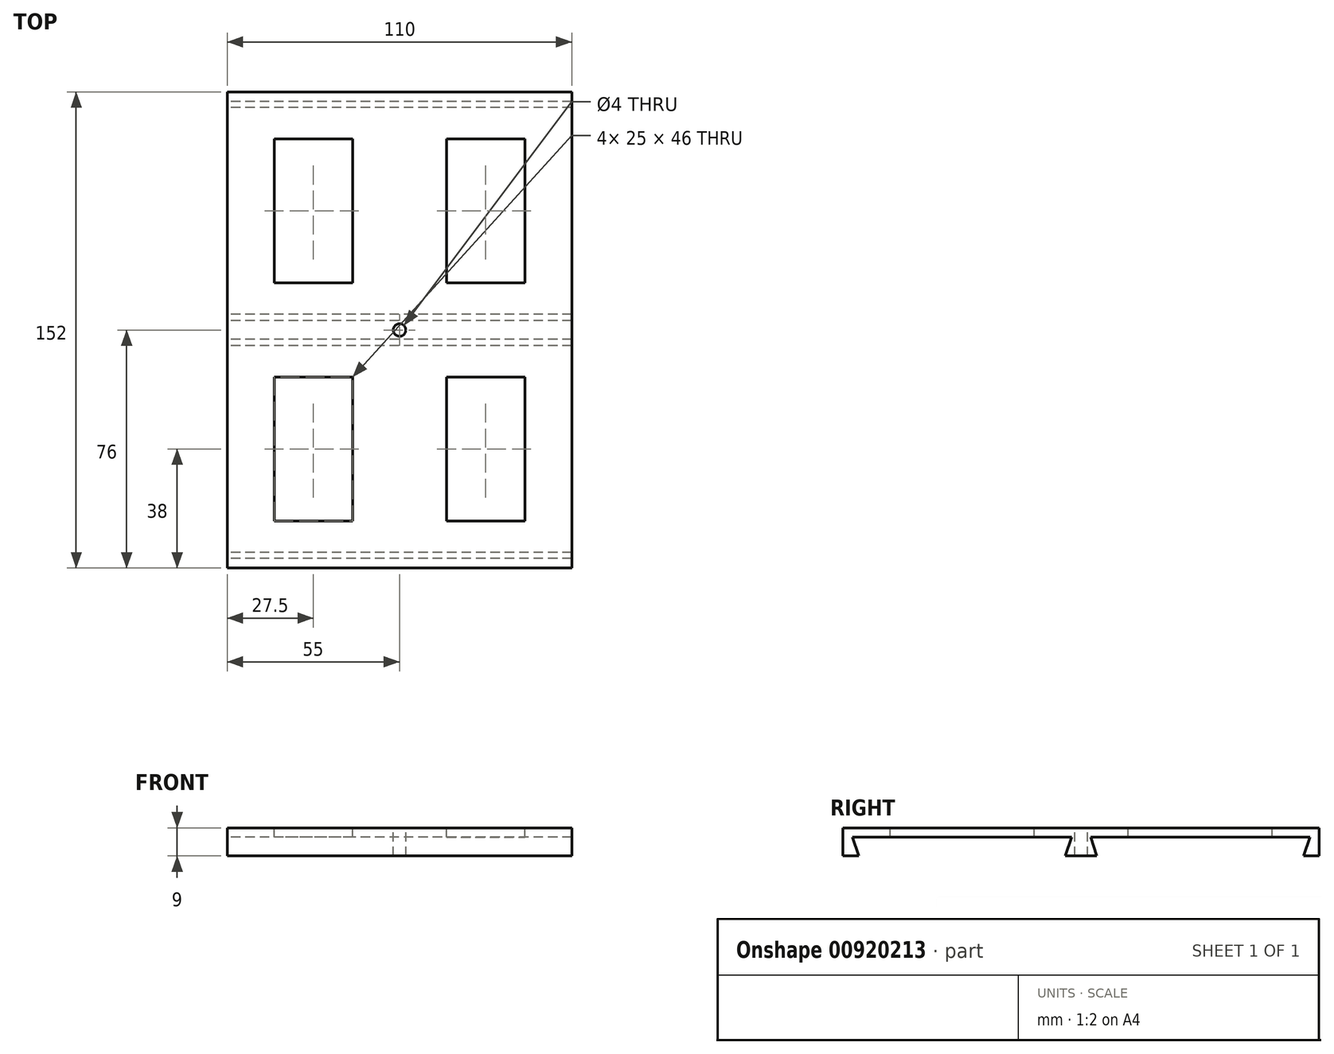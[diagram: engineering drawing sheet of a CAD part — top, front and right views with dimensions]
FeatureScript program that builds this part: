
annotation { "Feature Type Name" : "Feature", "Feature Type Description" : "" }
export const myFeature = defineFeature(function(context is Context, id is Id, definition is map)
    precondition{}
    {
        {
            var Q0;
            Q0=qCreatedBy(makeId("Right.planeOp"),FACE);
            var sketch = newSketch(context, id + "F0", { "sketchPlane" : qUnion([Q0])});
            skLineSegment(sketch, "E0", {"start": v(0, -9) * mm, "end": v(-5, -9) * mm});
            skLineSegment(sketch, "E1", {"start": v(0, 0) * mm, "end": v(-76, 0) * mm});
            skLineSegment(sketch, "E2", {"start": v(0, 0) * mm, "end": v(-3, 0) * mm});
            skLineSegment(sketch, "E3", {"start": v(-3, -3) * mm, "end": v(-5, -9) * mm});
            skLineSegment(sketch, "E4", {"start": v(-3, -3) * mm, "end": v(-73, -3) * mm});
            skLineSegment(sketch, "E5", {"start": v(-73, -9) * mm, "end": v(-71, -9) * mm});
            skLineSegment(sketch, "E6", {"start": v(-71, -9) * mm, "end": v(-73, -3) * mm});
            skLineSegment(sketch, "E7", {"start": v(-76, 0) * mm, "end": v(-76, -9) * mm});
            skLineSegment(sketch, "E8", {"start": v(-76, -9) * mm, "end": v(-73, -9) * mm});
            skLineSegment(sketch, "E9.MirrorCS", {"start": v(0, 0) * mm, "end": v(3, 0) * mm});
            skLineSegment(sketch, "E10.MirrorCS", {"start": v(73, -9) * mm, "end": v(71, -9) * mm});
            skLineSegment(sketch, "E11.MirrorCS", {"start": v(0, -9) * mm, "end": v(5, -9) * mm});
            skLineSegment(sketch, "E12.MirrorCS", {"start": v(76, -9) * mm, "end": v(73, -9) * mm});
            skLineSegment(sketch, "E13.MirrorCS", {"start": v(3, -3) * mm, "end": v(73, -3) * mm});
            skLineSegment(sketch, "E14.MirrorCS", {"start": v(71, -9) * mm, "end": v(73, -3) * mm});
            skLineSegment(sketch, "E15.MirrorCS", {"start": v(3, -3) * mm, "end": v(5, -9) * mm});
            skLineSegment(sketch, "E16.MirrorCS", {"start": v(76, 0) * mm, "end": v(76, -9) * mm});
            skLineSegment(sketch, "E17.MirrorCS", {"start": v(0, 0) * mm, "end": v(76, 0) * mm});
            skSolve(sketch);
        }
        {
            var Q0;
            Q0=makeQuery(id+"F0.imprint","IMPRINT",FACE,{"disambiguationData":[TD([[makeQuery(id+"F0.imprint","IMPRINT",EDGE,{"derivedFrom":sQuery(id+"F0.wireOp",EDGE,"E0")}),-1.0]])]});
            extrude(context, id + "F1", {"entities" : qUnion([Q0]), "depth" : 110 * mm, "offsetDistance" : 25 * mm});
        }
        {
            var Q0;
            Q0=makeQuery(id+"F1.opExtrude","SWEPT_FACE",FACE,{"disambiguationData":[OSD([sQuery(id+"F0.wireOp",EDGE,"E1"),sQuery(id+"F0.wireOp",EDGE,"E2"),sQuery(id+"F0.wireOp",EDGE,"E17.MirrorCS")])]});
            var sketch = newSketch(context, id + "F2", { "sketchPlane" : qUnion([Q0])});
            skLineSegment(sketch, "E18", {"start": v(0, 0) * mm, "end": v(110, 0) * mm, "construction": true});
            skLineSegment(sketch, "E19", {"start": v(55, -76) * mm, "end": v(55, 76) * mm, "construction": true});
            skLineSegment(sketch, "E20", {"start": v(0, -76) * mm, "end": v(0, -61) * mm, "construction": true});
            skLineSegment(sketch, "E21", {"start": v(0, -61) * mm, "end": v(15, -61) * mm, "construction": true});
            skLineSegment(sketch, "E22", {"start": v(55, 0) * mm, "end": v(40, 0) * mm});
            skLineSegment(sketch, "E23", {"start": v(40, 0) * mm, "end": v(40, -15) * mm});
            skLineSegment(sketch, "E24.bottom", {"start": v(15, -61) * mm, "end": v(40, -61) * mm});
            skLineSegment(sketch, "E24.top", {"start": v(15, -15) * mm, "end": v(40, -15) * mm});
            skLineSegment(sketch, "E24.left", {"start": v(15, -61) * mm, "end": v(15, -15) * mm});
            skLineSegment(sketch, "E24.right", {"start": v(40, -61) * mm, "end": v(40, -15) * mm});
            skCircle(sketch, "E25", {"center": v(55, 0) * mm, "radius": 2 * mm});
            skLineSegment(sketch, "E26.MirrorCS", {"start": v(70, -61) * mm, "end": v(70, -15) * mm});
            skLineSegment(sketch, "E27.MirrorCS", {"start": v(95, -15) * mm, "end": v(70, -15) * mm});
            skLineSegment(sketch, "E28.MirrorCS", {"start": v(95, -61) * mm, "end": v(95, -15) * mm});
            skLineSegment(sketch, "E29.MirrorCS", {"start": v(95, -61) * mm, "end": v(70, -61) * mm});
            skLineSegment(sketch, "E30.MirrorCS", {"start": v(95, 15) * mm, "end": v(70, 15) * mm});
            skLineSegment(sketch, "E31.MirrorCS", {"start": v(95, 61) * mm, "end": v(95, 15) * mm});
            skLineSegment(sketch, "E32.MirrorCS", {"start": v(70, 61) * mm, "end": v(70, 15) * mm});
            skLineSegment(sketch, "E33.MirrorCS", {"start": v(95, 61) * mm, "end": v(70, 61) * mm});
            skLineSegment(sketch, "E34.MirrorCS", {"start": v(15, 15) * mm, "end": v(40, 15) * mm});
            skLineSegment(sketch, "E35.MirrorCS", {"start": v(40, 61) * mm, "end": v(40, 15) * mm});
            skLineSegment(sketch, "E36.MirrorCS", {"start": v(15, 61) * mm, "end": v(40, 61) * mm});
            skLineSegment(sketch, "E37.MirrorCS", {"start": v(15, 61) * mm, "end": v(15, 15) * mm});
            skSolve(sketch);
        }
        {
            var Q0;
            Q0=makeQuery(id+"F2.imprint","IMPRINT",FACE,{"disambiguationData":[TD([[makeQuery(id+"F2.imprint","IMPRINT",EDGE,{"derivedFrom":sQuery(id+"F2.wireOp",EDGE,"E24.bottom")}),1.0]])]});
            var Q1;
            Q1=makeQuery(id+"F2.imprint","IMPRINT",FACE,{"disambiguationData":[TD([[makeQuery(id+"F2.imprint","IMPRINT",EDGE,{"derivedFrom":sQuery(id+"F2.wireOp",EDGE,"E26.MirrorCS")}),-1.0]])]});
            var Q2;
            Q2=makeQuery(id+"F2.imprint","IMPRINT",FACE,{"disambiguationData":[TD([[makeQuery(id+"F2.imprint","IMPRINT",EDGE,{"derivedFrom":sQuery(id+"F2.wireOp",EDGE,"E30.MirrorCS")}),-1.0]])]});
            var Q3;
            Q3=makeQuery(id+"F2.imprint","IMPRINT",FACE,{"disambiguationData":[TD([[makeQuery(id+"F2.imprint","IMPRINT",EDGE,{"derivedFrom":sQuery(id+"F2.wireOp",EDGE,"E34.MirrorCS")}),1.0]])]});
            var Q4;
            Q4=makeQuery(id+"F2.imprint","IMPRINT",FACE,{"disambiguationData":[TD([[makeQuery(id+"F2.imprint","IMPRINT",EDGE,{"derivedFrom":sQuery(id+"F2.wireOp",EDGE,"E25")}),1.0]])]});
            extrude(context, id + "F3", {"entities" : qUnion([Q0, Q1, Q2, Q3, Q4]), "operationType" : NewBodyOperationType.REMOVE, "depth" : -25 * mm, "offsetDistance" : 25 * mm});
        }
    });
